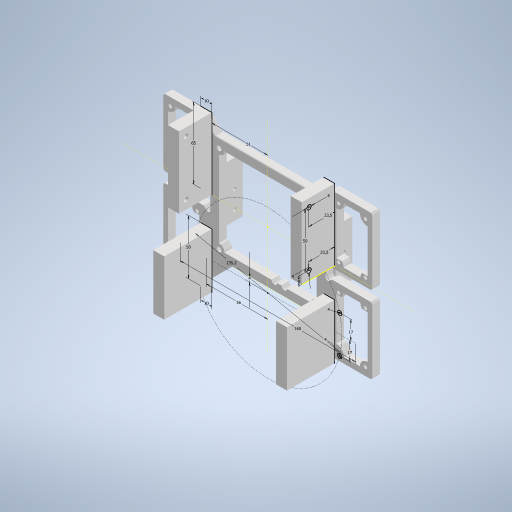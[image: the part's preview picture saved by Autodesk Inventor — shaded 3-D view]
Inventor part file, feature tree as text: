
AUTODESK INVENTOR PART (.ipt)
format: ipt  version: 2024.2 (Build 282272000, 272)  size: 794,624 bytes
history: native  units: mm
features: extrude x6, fillet x5, sketch x5, other x1
ambient origin geometry x8: Origin, YZ Plane, XZ Plane, XY Plane, X Axis, Y Axis, Z Axis, Center Point
bodies: Body1 (feature_tree)
feature tree (17):
  other  "Bryła1"
  extrude  "Wyciągnięcie proste1"  Depth=105.0mm
  fillet  "Zaokrąglenie1"  Radius=96.0mm
  extrude  "Wyciągnięcie proste2"  Depth=7.0mm TaperAngle=0.0deg
  fillet  "Zaokrąglenie2"  Radius=89.0mm
  extrude  "Wyciągnięcie proste3"  Depth=80.0mm
  sketch  "Szkic4"
  extrude  "Wyciągnięcie proste4"  Depth=2.5mm
  fillet  "Zaokrąglenie3"  Radius=15.0mm
  fillet  "Zaokrąglenie4"  Radius=2.5mm
  extrude  "Wyciągnięcie proste5"  Depth=9.0mm
  extrude  "Wyciągnięcie proste6"  Depth=5.0mm
  fillet  "Zaokrąglenie5"  Radius=5.0mm
  sketch  "Szkic1"
  sketch  "Szkic2"
  sketch  "Szkic3"
  sketch  "Szkic5"
